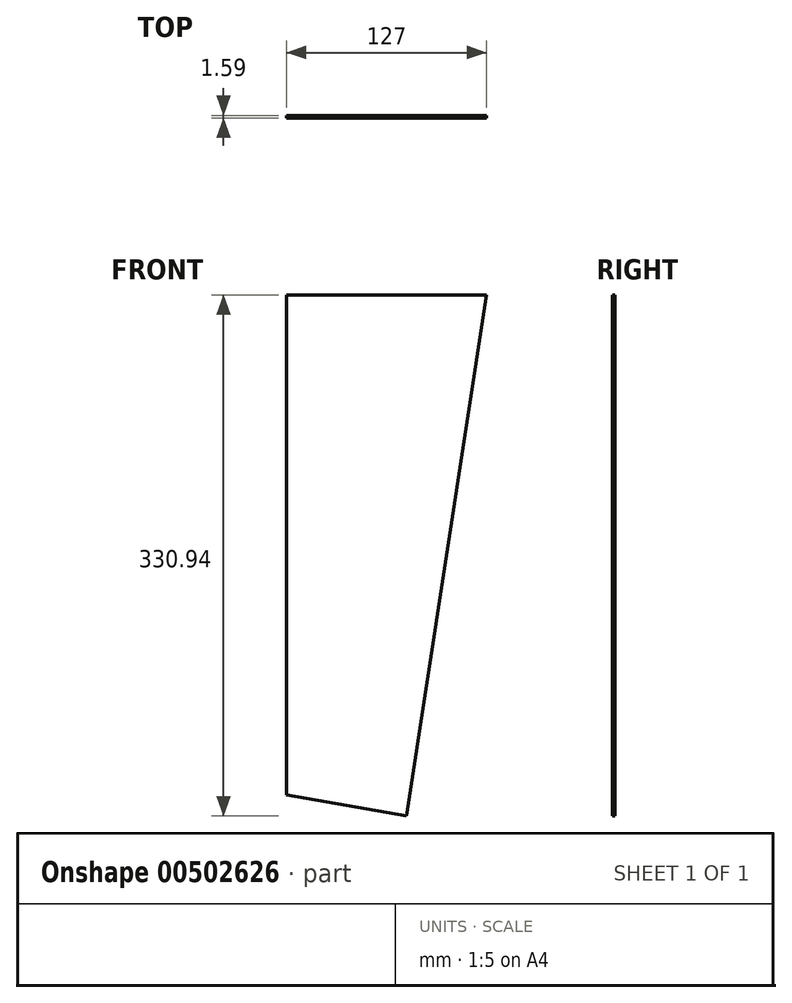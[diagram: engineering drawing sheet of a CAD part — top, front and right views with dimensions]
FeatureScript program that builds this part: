
annotation { "Feature Type Name" : "Feature", "Feature Type Description" : "" }
export const myFeature = defineFeature(function(context is Context, id is Id, definition is map)
    precondition{}
    {
        {
            var Q0;
            Q0=qCreatedBy(makeId("Front.planeOp"),FACE);
            var sketch = newSketch(context, id + "F0", { "sketchPlane" : qUnion([Q0])});
            skLineSegment(sketch, "E0", {"start": v(0, 0) * mm, "end": v(0, 317.5) * mm});
            skLineSegment(sketch, "E1", {"start": v(0, 317.5) * mm, "end": v(127, 317.5) * mm});
            skLineSegment(sketch, "E2", {"start": v(127, 317.5) * mm, "end": v(76.2, -13.44) * mm});
            skLineSegment(sketch, "E3", {"start": v(76.2, -13.44) * mm, "end": v(0, 0) * mm});
            skSolve(sketch);
        }
        {
            var Q0;
            Q0=makeQuery(id+"F0.imprint","IMPRINT",FACE,{"disambiguationData":[TD([[makeQuery(id+"F0.imprint","IMPRINT",EDGE,{"derivedFrom":sQuery(id+"F0.wireOp",EDGE,"E0")}),-1.0]])]});
            extrude(context, id + "F1", {"entities" : qUnion([Q0]), "depth" : 1.59 * mm});
        }
    });
